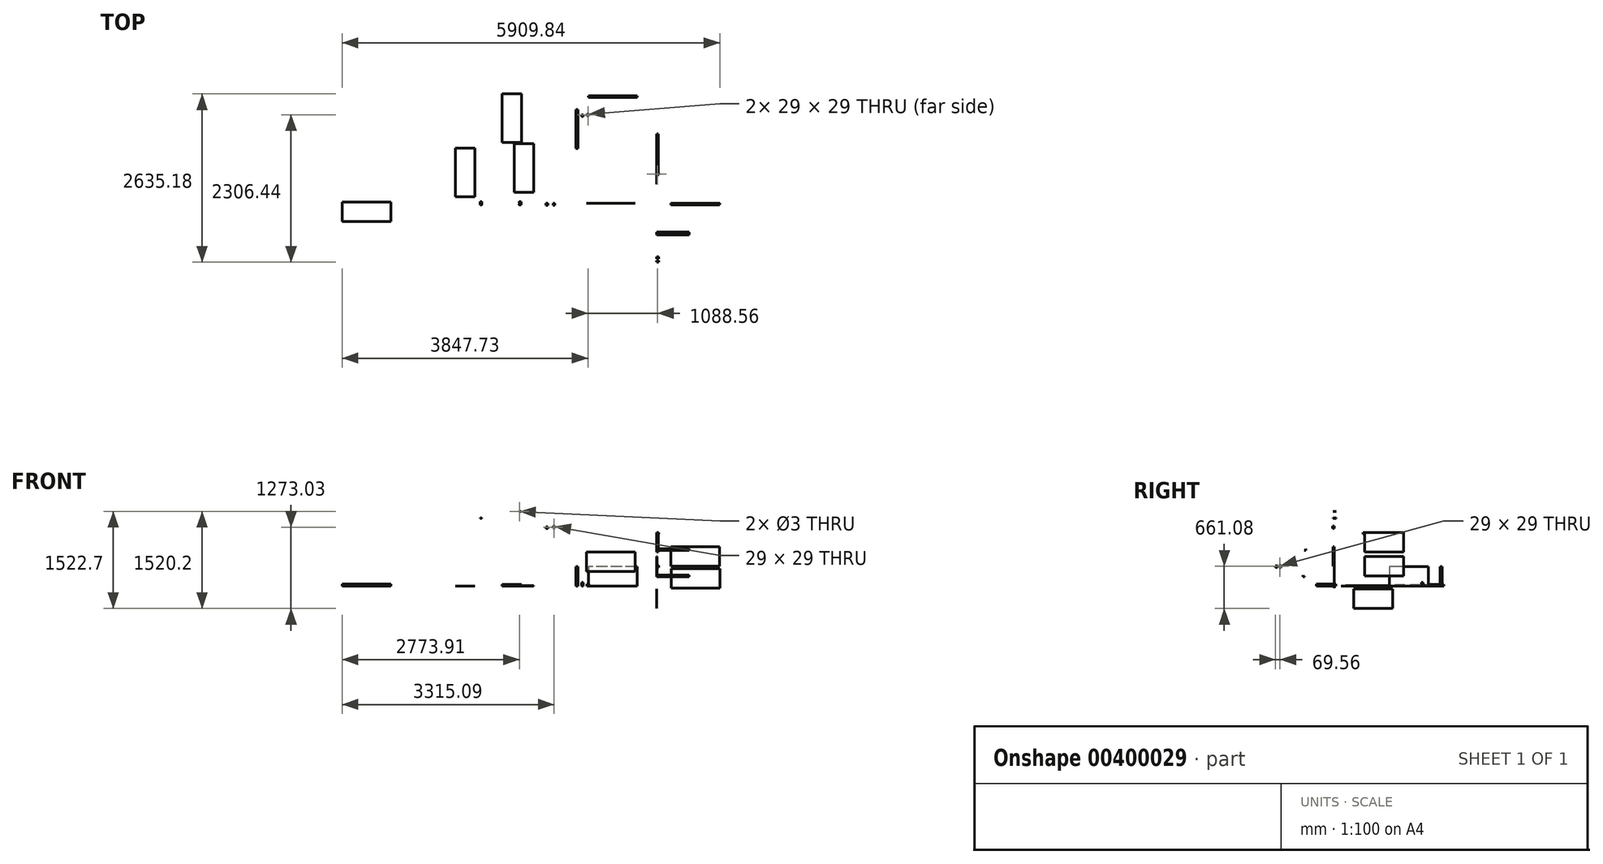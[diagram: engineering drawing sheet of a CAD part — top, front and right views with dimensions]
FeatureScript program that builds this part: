
annotation { "Feature Type Name" : "Feature", "Feature Type Description" : "" }
export const myFeature = defineFeature(function(context is Context, id is Id, definition is map)
    precondition{}
    {
        {
            var Q0;
            Q0=qCreatedBy(makeId("Front.planeOp"),FACE);
            var sketch = newSketch(context, id + "F0", { "sketchPlane" : qUnion([Q0])});
            skLineSegment(sketch, "E0.bottom", {"start": v(980.84, 309.69) * mm, "end": v(218.84, 309.69) * mm});
            skLineSegment(sketch, "E0.top", {"start": v(980.84, 614.49) * mm, "end": v(218.84, 614.49) * mm});
            skLineSegment(sketch, "E0.left", {"start": v(980.84, 309.69) * mm, "end": v(980.84, 614.49) * mm});
            skLineSegment(sketch, "E0.right", {"start": v(218.84, 309.69) * mm, "end": v(218.84, 614.49) * mm});
            skPoint(sketch, "E0.middle", {"position": v(599.84, 462.09) * mm});
            skSolve(sketch);
        }
        {
            var Q0;
            Q0=makeQuery(id+"F0.imprint","IMPRINT",FACE,{"disambiguationData":[TD([[makeQuery(id+"F0.imprint","IMPRINT",EDGE,{"derivedFrom":sQuery(id+"F0.wireOp",EDGE,"E0.bottom")}),-1.0]])]});
            extrude(context, id + "F1", {"entities" : qUnion([Q0]), "depth" : 25 * mm});
        }
        {
            var Q0;
            Q0=qCreatedBy(makeId("Front.planeOp"),FACE);
            var sketch = newSketch(context, id + "F2", { "sketchPlane" : qUnion([Q0])});
            skLineSegment(sketch, "E1.bottom", {"start": v(986.05, -29.83) * mm, "end": v(224.05, -29.83) * mm});
            skLineSegment(sketch, "E1.top", {"start": v(986.05, 274.97) * mm, "end": v(224.05, 274.97) * mm});
            skLineSegment(sketch, "E1.left", {"start": v(986.05, -29.83) * mm, "end": v(986.05, 274.97) * mm});
            skLineSegment(sketch, "E1.right", {"start": v(224.05, -29.83) * mm, "end": v(224.05, 274.97) * mm});
            skPoint(sketch, "E1.middle", {"position": v(605.05, 122.57) * mm});
            skSolve(sketch);
        }
        {
            var Q0;
            Q0=makeQuery(id+"F2.imprint","IMPRINT",FACE,{"disambiguationData":[TD([[makeQuery(id+"F2.imprint","IMPRINT",EDGE,{"derivedFrom":sQuery(id+"F2.wireOp",EDGE,"E1.bottom")}),-1.0]])]});
            extrude(context, id + "F3", {"entities" : qUnion([Q0]), "depth" : 4 * mm});
        }
        {
            var Q0;
            Q0=qCreatedBy(makeId("Front.planeOp"),FACE);
            var sketch = newSketch(context, id + "F4", { "sketchPlane" : qUnion([Q0])});
            skLineSegment(sketch, "E2.bottom", {"start": v(-340.18, 230.94) * mm, "end": v(-1102.18, 230.94) * mm});
            skLineSegment(sketch, "E2.top", {"start": v(-340.18, 535.74) * mm, "end": v(-1102.18, 535.74) * mm});
            skLineSegment(sketch, "E2.left", {"start": v(-340.18, 230.94) * mm, "end": v(-340.18, 535.74) * mm});
            skLineSegment(sketch, "E2.right", {"start": v(-1102.18, 230.94) * mm, "end": v(-1102.18, 535.74) * mm});
            skPoint(sketch, "E2.middle", {"position": v(-721.18, 383.34) * mm});
            skSolve(sketch);
        }
        {
            var Q0;
            Q0=makeQuery(id+"F4.imprint","IMPRINT",FACE,{"disambiguationData":[TD([[makeQuery(id+"F4.imprint","IMPRINT",EDGE,{"derivedFrom":sQuery(id+"F4.wireOp",EDGE,"E2.bottom")}),-1.0]])]});
            extrude(context, id + "F5", {"entities" : qUnion([Q0]), "depth" : 1 * mm});
        }
        {
            var Q0;
            Q0=qCreatedBy(makeId("Right.planeOp"),FACE);
            var sketch = newSketch(context, id + "F6", { "sketchPlane" : qUnion([Q0])});
            skLineSegment(sketch, "E3.bottom", {"start": v(1084.04, 535.01) * mm, "end": v(474.44, 535.01) * mm});
            skLineSegment(sketch, "E3.top", {"start": v(1084.04, 839.81) * mm, "end": v(474.44, 839.81) * mm});
            skLineSegment(sketch, "E3.left", {"start": v(1084.04, 535.01) * mm, "end": v(1084.04, 839.81) * mm});
            skLineSegment(sketch, "E3.right", {"start": v(474.44, 535.01) * mm, "end": v(474.44, 839.81) * mm});
            skPoint(sketch, "E3.middle", {"position": v(779.24, 687.41) * mm});
            skSolve(sketch);
        }
        {
            var Q0;
            Q0=makeQuery(id+"F6.imprint","IMPRINT",FACE,{"disambiguationData":[TD([[makeQuery(id+"F6.imprint","IMPRINT",EDGE,{"derivedFrom":sQuery(id+"F6.wireOp",EDGE,"E3.bottom")}),-1.0]])]});
            extrude(context, id + "F7", {"entities" : qUnion([Q0]), "depth" : 25 * mm});
        }
        {
            var Q0;
            Q0=qCreatedBy(makeId("Right.planeOp"),FACE);
            var sketch = newSketch(context, id + "F8", { "sketchPlane" : qUnion([Q0])});
            skLineSegment(sketch, "E4.bottom", {"start": v(1082.3, 157.36) * mm, "end": v(472.7, 157.36) * mm});
            skLineSegment(sketch, "E4.top", {"start": v(1082.3, 462.16) * mm, "end": v(472.7, 462.16) * mm});
            skLineSegment(sketch, "E4.left", {"start": v(1082.3, 157.36) * mm, "end": v(1082.3, 462.16) * mm});
            skLineSegment(sketch, "E4.right", {"start": v(472.7, 157.36) * mm, "end": v(472.7, 462.16) * mm});
            skPoint(sketch, "E4.middle", {"position": v(777.5, 309.76) * mm});
            skSolve(sketch);
        }
        {
            var Q0;
            Q0=makeQuery(id+"F8.imprint","IMPRINT",FACE,{"disambiguationData":[TD([[makeQuery(id+"F8.imprint","IMPRINT",EDGE,{"derivedFrom":sQuery(id+"F8.wireOp",EDGE,"E4.bottom")}),-1.0]])]});
            extrude(context, id + "F9", {"entities" : qUnion([Q0]), "depth" : 4 * mm});
        }
        {
            var Q0;
            Q0=qCreatedBy(makeId("Right.planeOp"),FACE);
            var sketch = newSketch(context, id + "F10", { "sketchPlane" : qUnion([Q0])});
            skLineSegment(sketch, "E5.bottom", {"start": v(910.2, -350.78) * mm, "end": v(300.6, -350.78) * mm});
            skLineSegment(sketch, "E5.top", {"start": v(910.2, -45.98) * mm, "end": v(300.6, -45.98) * mm});
            skLineSegment(sketch, "E5.left", {"start": v(910.2, -350.78) * mm, "end": v(910.2, -45.98) * mm});
            skLineSegment(sketch, "E5.right", {"start": v(300.6, -350.78) * mm, "end": v(300.6, -45.98) * mm});
            skPoint(sketch, "E5.middle", {"position": v(605.4, -198.38) * mm});
            skSolve(sketch);
        }
        {
            var Q0;
            Q0=makeQuery(id+"F10.imprint","IMPRINT",FACE,{"disambiguationData":[TD([[makeQuery(id+"F10.imprint","IMPRINT",EDGE,{"derivedFrom":sQuery(id+"F10.wireOp",EDGE,"E5.bottom")}),-1.0]])]});
            extrude(context, id + "F11", {"entities" : qUnion([Q0]), "depth" : 1 * mm});
        }
        {
            var Q0;
            Q0=qCreatedBy(makeId("Right.planeOp"),FACE);
            var sketch = newSketch(context, id + "F12", { "sketchPlane" : qUnion([Q0])});
            skLineSegment(sketch, "E6", {"start": v(-495.1, 174.65) * mm, "end": v(-495.1, 149.25) * mm});
            skLineSegment(sketch, "E7", {"start": v(-495.1, 149.25) * mm, "end": v(-469.7, 149.25) * mm});
            skLineSegment(sketch, "E8", {"start": v(-469.7, 149.25) * mm, "end": v(-469.7, 151.25) * mm});
            skLineSegment(sketch, "E9", {"start": v(-469.7, 151.25) * mm, "end": v(-493.1, 151.25) * mm});
            skLineSegment(sketch, "E10", {"start": v(-493.1, 151.25) * mm, "end": v(-493.1, 174.65) * mm});
            skLineSegment(sketch, "E11", {"start": v(-493.1, 174.65) * mm, "end": v(-495.1, 174.65) * mm});
            skSolve(sketch);
        }
        {
            var Q0;
            Q0=makeQuery(id+"F12.imprint","IMPRINT",FACE,{"disambiguationData":[TD([[makeQuery(id+"F12.imprint","IMPRINT",EDGE,{"derivedFrom":sQuery(id+"F12.wireOp",EDGE,"E6")}),1.0]])]});
            extrude(context, id + "F13", {"entities" : qUnion([Q0]), "depth" : 508 * mm});
        }
        {
            var Q0;
            Q0=qCreatedBy(makeId("Right.planeOp"),FACE);
            var sketch = newSketch(context, id + "F14", { "sketchPlane" : qUnion([Q0])});
            skLineSegment(sketch, "E12", {"start": v(-447.15, 585.76) * mm, "end": v(-447.15, 560.36) * mm});
            skLineSegment(sketch, "E13", {"start": v(-447.15, 560.36) * mm, "end": v(-472.55, 560.36) * mm});
            skLineSegment(sketch, "E14", {"start": v(-472.55, 560.36) * mm, "end": v(-472.55, 562.36) * mm});
            skLineSegment(sketch, "E15", {"start": v(-472.55, 562.36) * mm, "end": v(-449.15, 562.36) * mm});
            skLineSegment(sketch, "E16", {"start": v(-449.15, 562.36) * mm, "end": v(-449.15, 585.76) * mm});
            skLineSegment(sketch, "E17", {"start": v(-449.15, 585.76) * mm, "end": v(-447.15, 585.76) * mm});
            skSolve(sketch);
        }
        {
            var Q0;
            Q0=makeQuery(id+"F14.imprint","IMPRINT",FACE,{"disambiguationData":[TD([[makeQuery(id+"F14.imprint","IMPRINT",EDGE,{"derivedFrom":sQuery(id+"F14.wireOp",EDGE,"E12")}),-1.0]])]});
            var Q1;
            Q1=sQuery(id+"F14.wireOp",EDGE,"E15");
            extrude(context, id + "F15", {"entities" : qUnion([Q0]), "surfaceEntities" : qUnion([Q1]), "depth" : 508 * mm});
        }
        {
            var Q0;
            Q0=qCreatedBy(makeId("Top.planeOp"),FACE);
            var sketch = newSketch(context, id + "F16", { "sketchPlane" : qUnion([Q0])});
            skLineSegment(sketch, "E18.bottom", {"start": v(-2119.67, 951.73) * mm, "end": v(-2424.47, 951.73) * mm});
            skLineSegment(sketch, "E18.top", {"start": v(-2119.67, 1713.73) * mm, "end": v(-2424.47, 1713.73) * mm});
            skLineSegment(sketch, "E18.left", {"start": v(-2119.67, 951.73) * mm, "end": v(-2119.67, 1713.73) * mm});
            skLineSegment(sketch, "E18.right", {"start": v(-2424.47, 951.73) * mm, "end": v(-2424.47, 1713.73) * mm});
            skPoint(sketch, "E18.middle", {"position": v(-2272.07, 1332.73) * mm});
            skSolve(sketch);
        }
        {
            var Q0;
            Q0=makeQuery(id+"F16.imprint","IMPRINT",FACE,{"disambiguationData":[TD([[makeQuery(id+"F16.imprint","IMPRINT",EDGE,{"derivedFrom":sQuery(id+"F16.wireOp",EDGE,"E18.bottom")}),-1.0]])]});
            extrude(context, id + "F17", {"entities" : qUnion([Q0]), "depth" : 25 * mm});
        }
        {
            var Q0;
            Q0=qCreatedBy(makeId("Top.planeOp"),FACE);
            var sketch = newSketch(context, id + "F18", { "sketchPlane" : qUnion([Q0])});
            skLineSegment(sketch, "E19.bottom", {"start": v(-2849.46, 102.13) * mm, "end": v(-3154.26, 102.13) * mm});
            skLineSegment(sketch, "E19.top", {"start": v(-2849.46, 864.13) * mm, "end": v(-3154.26, 864.13) * mm});
            skLineSegment(sketch, "E19.left", {"start": v(-2849.46, 102.13) * mm, "end": v(-2849.46, 864.13) * mm});
            skLineSegment(sketch, "E19.right", {"start": v(-3154.26, 102.13) * mm, "end": v(-3154.26, 864.13) * mm});
            skPoint(sketch, "E19.middle", {"position": v(-3001.86, 483.13) * mm});
            skSolve(sketch);
        }
        {
            var Q0;
            Q0=makeQuery(id+"F18.imprint","IMPRINT",FACE,{"disambiguationData":[TD([[makeQuery(id+"F18.imprint","IMPRINT",EDGE,{"derivedFrom":sQuery(id+"F18.wireOp",EDGE,"E19.bottom")}),-1.0]])]});
            extrude(context, id + "F19", {"entities" : qUnion([Q0]), "depth" : 1 * mm});
        }
        {
            var Q0;
            Q0=qCreatedBy(makeId("Top.planeOp"),FACE);
            var sketch = newSketch(context, id + "F20", { "sketchPlane" : qUnion([Q0])});
            skLineSegment(sketch, "E20.bottom", {"start": v(-1923.09, 173.05) * mm, "end": v(-2227.89, 173.05) * mm});
            skLineSegment(sketch, "E20.top", {"start": v(-1923.09, 935.05) * mm, "end": v(-2227.89, 935.05) * mm});
            skLineSegment(sketch, "E20.left", {"start": v(-1923.09, 173.05) * mm, "end": v(-1923.09, 935.05) * mm});
            skLineSegment(sketch, "E20.right", {"start": v(-2227.89, 173.05) * mm, "end": v(-2227.89, 935.05) * mm});
            skPoint(sketch, "E20.middle", {"position": v(-2075.49, 554.05) * mm});
            skSolve(sketch);
        }
        {
            var Q0;
            Q0=makeQuery(id+"F20.imprint","IMPRINT",FACE,{"disambiguationData":[TD([[makeQuery(id+"F20.imprint","IMPRINT",EDGE,{"derivedFrom":sQuery(id+"F20.wireOp",EDGE,"E20.bottom")}),-1.0]])]});
            extrude(context, id + "F21", {"entities" : qUnion([Q0]), "depth" : 4 * mm});
        }
        {
            var Q0;
            Q0=qCreatedBy(makeId("Front.planeOp"),FACE);
            var sketch = newSketch(context, id + "F22", { "sketchPlane" : qUnion([Q0])});
            skCircle(sketch, "E21", {"center": v(-2743.03, 1064.39) * mm, "radius": 2.5 * mm});
            skCircle(sketch, "E22", {"center": v(-2743.03, 1064.39) * mm, "radius": 1.5 * mm});
            skSolve(sketch);
        }
        {
            var Q0;
            Q0=makeQuery(id+"F22.imprint","IMPRINT",FACE,{"disambiguationData":[TD([[makeQuery(id+"F22.imprint","IMPRINT",EDGE,{"derivedFrom":sQuery(id+"F22.wireOp",EDGE,"E21")}),1.0]])]});
            extrude(context, id + "F23", {"entities" : qUnion([Q0]), "endBound" : BoundingType.SYMMETRIC, "depth" : 25.4 * mm});
        }
        {
            var Q0;
            Q0=makeQuery(id+"F22.imprint","IMPRINT",FACE,{"disambiguationData":[TD([[makeQuery(id+"F22.imprint","IMPRINT",EDGE,{"derivedFrom":sQuery(id+"F22.wireOp",EDGE,"E22")}),1.0]])]});
            extrude(context, id + "F24", {"entities" : qUnion([Q0]), "operationType" : NewBodyOperationType.ADD, "endBound" : BoundingType.SYMMETRIC, "depth" : 50.8 * mm});
        }
        {
            var Q0;
            Q0=makeQuery(id+"F23.opExtrude","CAP_FACE",FACE,{"disambiguationData":[OSD([sQuery(id+"F22.wireOp",EDGE,"E21"),sQuery(id+"F22.wireOp",EDGE,"E22")])],"isStart":true});
            var sketch = newSketch(context, id + "F25", { "sketchPlane" : qUnion([Q0])});
            skLineSegment(sketch, "E23", {"start": v(2744.81, 1066.14) * mm, "end": v(2744.81, 1062.64) * mm});
            skLineSegment(sketch, "E24", {"start": v(2744.81, 1062.64) * mm, "end": v(2746.81, 1062.64) * mm});
            skLineSegment(sketch, "E25", {"start": v(2746.81, 1062.64) * mm, "end": v(2746.81, 1066.14) * mm});
            skLineSegment(sketch, "E26", {"start": v(2746.81, 1066.14) * mm, "end": v(2744.81, 1066.14) * mm});
            skSolve(sketch);
        }
        {
            var Q0;
            {var subQ0=sQuery(id+"F25.wireOp",EDGE,"E24");Q0=makeQuery(id+"F25.imprint","IMPRINT",FACE,{"disambiguationData":[TD([[makeQuery(id+"F25.imprint","IMPRINT",EDGE,{"derivedFrom":subQ0}),1.0]])]});}
            extrude(context, id + "F26", {"entities" : qUnion([Q0]), "oppositeDirection" : true, "depth" : 25.4 * mm});
        }
        {
            var Q0;
            Q0=makeQuery(id+"F22.imprint","IMPRINT",FACE,{"disambiguationData":[TD([[makeQuery(id+"F22.imprint","IMPRINT",EDGE,{"derivedFrom":sQuery(id+"F22.wireOp",EDGE,"E21")}),1.0]])]});
            var sketch = newSketch(context, id + "F27", { "sketchPlane" : qUnion([Q0])});
            skLineSegment(sketch, "E27.bottom", {"start": v(-2746.81, 1066.14) * mm, "end": v(-2765.86, 1066.14) * mm});
            skLineSegment(sketch, "E27.top", {"start": v(-2746.81, 1062.64) * mm, "end": v(-2765.86, 1062.64) * mm});
            skLineSegment(sketch, "E27.left", {"start": v(-2746.81, 1066.14) * mm, "end": v(-2746.81, 1062.64) * mm});
            skLineSegment(sketch, "E27.right", {"start": v(-2765.86, 1066.14) * mm, "end": v(-2765.86, 1062.64) * mm});
            skSolve(sketch);
        }
        {
            var Q0;
            Q0=makeQuery(id+"F27.imprint","IMPRINT",FACE,{"disambiguationData":[TD([[makeQuery(id+"F27.imprint","IMPRINT",EDGE,{"derivedFrom":sQuery(id+"F27.wireOp",EDGE,"E27.bottom")}),1.0]])]});
            extrude(context, id + "F28", {"entities" : qUnion([Q0]), "operationType" : NewBodyOperationType.ADD, "endBound" : BoundingType.SYMMETRIC, "depth" : 50.8 * mm});
        }
        {
            var Q0;
            Q0=qCreatedBy(makeId("Front.planeOp"),FACE);
            var sketch = newSketch(context, id + "F29", { "sketchPlane" : qUnion([Q0])});
            skCircle(sketch, "E28", {"center": v(-2149.88, 1169.42) * mm, "radius": 2.5 * mm});
            skCircle(sketch, "E29", {"center": v(-2149.88, 1169.42) * mm, "radius": 1.5 * mm});
            skSolve(sketch);
        }
        {
            var Q0;
            Q0=makeQuery(id+"F29.imprint","IMPRINT",FACE,{"disambiguationData":[TD([[makeQuery(id+"F29.imprint","IMPRINT",EDGE,{"derivedFrom":sQuery(id+"F29.wireOp",EDGE,"E28")}),1.0]])]});
            extrude(context, id + "F30", {"entities" : qUnion([Q0]), "endBound" : BoundingType.SYMMETRIC, "depth" : 50.8 * mm});
        }
        {
            var Q0;
            Q0=makeQuery(id+"F29.imprint","IMPRINT",FACE,{"disambiguationData":[TD([[makeQuery(id+"F29.imprint","IMPRINT",EDGE,{"derivedFrom":sQuery(id+"F29.wireOp",EDGE,"E28")}),1.0]])]});
            extrude(context, id + "F31", {"entities" : qUnion([Q0]), "operationType" : NewBodyOperationType.REMOVE, "endBound" : BoundingType.SYMMETRIC, "oppositeDirection" : true, "depth" : 25.4 * mm});
        }
        {
            var Q0;
            Q0=makeQuery(id+"F29.imprint","IMPRINT",FACE,{"disambiguationData":[TD([[makeQuery(id+"F29.imprint","IMPRINT",EDGE,{"derivedFrom":sQuery(id+"F29.wireOp",EDGE,"E29")}),1.0]])]});
            var sketch = newSketch(context, id + "F32", { "sketchPlane" : qUnion([Q0])});
            skLineSegment(sketch, "E30", {"start": v(-2148.18, 1171.13) * mm, "end": v(-2148.18, 1167.63) * mm});
            skLineSegment(sketch, "E31", {"start": v(-2148.18, 1167.63) * mm, "end": v(-2146.18, 1167.63) * mm});
            skLineSegment(sketch, "E32", {"start": v(-2146.18, 1167.63) * mm, "end": v(-2146.18, 1171.13) * mm});
            skLineSegment(sketch, "E33", {"start": v(-2146.18, 1171.13) * mm, "end": v(-2148.18, 1171.13) * mm});
            skSolve(sketch);
        }
        {
            var Q0;
            Q0=makeQuery(id+"F32.imprint","IMPRINT",FACE,{"disambiguationData":[TD([[makeQuery(id+"F32.imprint","IMPRINT",EDGE,{"derivedFrom":sQuery(id+"F32.wireOp",EDGE,"E30")}),1.0]])]});
            extrude(context, id + "F33", {"entities" : qUnion([Q0]), "endBound" : BoundingType.SYMMETRIC, "depth" : 50.8 * mm});
        }
        {
            var Q0;
            Q0=makeQuery(id+"F32.imprint","IMPRINT",FACE,{"disambiguationData":[TD([[makeQuery(id+"F32.imprint","IMPRINT",EDGE,{"derivedFrom":sQuery(id+"F32.wireOp",EDGE,"E30")}),1.0]])]});
            extrude(context, id + "F34", {"entities" : qUnion([Q0]), "operationType" : NewBodyOperationType.REMOVE, "endBound" : BoundingType.SYMMETRIC, "oppositeDirection" : true, "depth" : 25.4 * mm});
        }
        {
            var Q0;
            Q0=makeQuery(id+"F33.opExtrude","CAP_FACE",FACE,{"disambiguationData":[OSD([sQuery(id+"F32.wireOp",EDGE,"E30"),sQuery(id+"F32.wireOp",EDGE,"E31"),sQuery(id+"F32.wireOp",EDGE,"E32"),sQuery(id+"F32.wireOp",EDGE,"E33")])],"isStart":false});
            var sketch = newSketch(context, id + "F35", { "sketchPlane" : qUnion([Q0])});
            skLineSegment(sketch, "E34.bottom", {"start": v(-2146.18, 1171.13) * mm, "end": v(-2120.78, 1171.13) * mm});
            skLineSegment(sketch, "E34.top", {"start": v(-2146.18, 1167.63) * mm, "end": v(-2120.78, 1167.63) * mm});
            skLineSegment(sketch, "E34.left", {"start": v(-2146.18, 1171.13) * mm, "end": v(-2146.18, 1167.63) * mm});
            skLineSegment(sketch, "E34.right", {"start": v(-2120.78, 1171.13) * mm, "end": v(-2120.78, 1167.63) * mm});
            skSolve(sketch);
        }
        {
            var Q0;
            Q0=makeQuery(id+"F35.imprint","IMPRINT",FACE,{"disambiguationData":[TD([[makeQuery(id+"F35.imprint","IMPRINT",EDGE,{"derivedFrom":sQuery(id+"F35.wireOp",EDGE,"E34.bottom")}),-1.0]])]});
            extrude(context, id + "F36", {"entities" : qUnion([Q0]), "oppositeDirection" : true, "depth" : 50.8 * mm});
        }
        {
            var Q0;
            Q0=makeQuery(id+"F7.opExtrude","SWEPT_FACE",FACE,{"disambiguationData":[OSD([sQuery(id+"F6.wireOp",EDGE,"E3.top")])]});
            var sketch = newSketch(context, id + "F37", { "sketchPlane" : qUnion([Q0])});
            skLineSegment(sketch, "E35.bottom", {"start": v(27.5, 444.44) * mm, "end": v(-2.5, 444.44) * mm});
            skLineSegment(sketch, "E35.top", {"start": v(27.5, 474.44) * mm, "end": v(-2.5, 474.44) * mm});
            skLineSegment(sketch, "E35.left", {"start": v(27.5, 444.44) * mm, "end": v(27.5, 474.44) * mm});
            skLineSegment(sketch, "E35.right", {"start": v(-2.5, 444.44) * mm, "end": v(-2.5, 474.44) * mm});
            skPoint(sketch, "E35.middle", {"position": v(12.5, 459.44) * mm});
            skLineSegment(sketch, "E36.bottom", {"start": v(27, 444.94) * mm, "end": v(-2, 444.94) * mm});
            skLineSegment(sketch, "E36.top", {"start": v(27, 473.94) * mm, "end": v(-2, 473.94) * mm});
            skLineSegment(sketch, "E36.left", {"start": v(27, 444.94) * mm, "end": v(27, 473.94) * mm});
            skLineSegment(sketch, "E36.right", {"start": v(-2, 444.94) * mm, "end": v(-2, 473.94) * mm});
            skSolve(sketch);
        }
        {
            var Q0;
            Q0=makeQuery(id+"F37.imprint","IMPRINT",FACE,{"disambiguationData":[TD([[makeQuery(id+"F37.imprint","IMPRINT",EDGE,{"derivedFrom":sQuery(id+"F37.wireOp",EDGE,"E35.bottom")}),-1.0]])]});
            extrude(context, id + "F38", {"entities" : qUnion([Q0]), "operationType" : NewBodyOperationType.ADD, "oppositeDirection" : true, "depth" : 25.4 * mm});
        }
        {
            var Q0;
            Q0=qCreatedBy(makeId("Top.planeOp"),FACE);
            var sketch = newSketch(context, id + "F39", { "sketchPlane" : qUnion([Q0])});
            skLineSegment(sketch, "E37.bottom", {"start": v(-1150.64, 1359.3) * mm, "end": v(-1178.64, 1359.3) * mm});
            skLineSegment(sketch, "E37.top", {"start": v(-1150.64, 1387.3) * mm, "end": v(-1178.64, 1387.3) * mm});
            skLineSegment(sketch, "E37.left", {"start": v(-1150.64, 1359.3) * mm, "end": v(-1150.64, 1387.3) * mm});
            skLineSegment(sketch, "E37.right", {"start": v(-1178.64, 1359.3) * mm, "end": v(-1178.64, 1387.3) * mm});
            skPoint(sketch, "E37.middle", {"position": v(-1164.64, 1373.3) * mm});
            skSolve(sketch);
        }
        {
            var Q0;
            Q0=makeQuery(id+"F39.imprint","IMPRINT",FACE,{"disambiguationData":[TD([[makeQuery(id+"F39.imprint","IMPRINT",EDGE,{"derivedFrom":sQuery(id+"F39.wireOp",EDGE,"E37.bottom")}),-1.0]])]});
            extrude(context, id + "F40", {"entities" : qUnion([Q0]), "depth" : 60 * mm});
        }
        {
            var Q0;
            Q0=qCreatedBy(makeId("Top.planeOp"),FACE);
            var sketch = newSketch(context, id + "F41", { "sketchPlane" : qUnion([Q0])});
            skLineSegment(sketch, "E38.bottom", {"start": v(-1061.06, 1370) * mm, "end": v(-1091.06, 1370) * mm});
            skLineSegment(sketch, "E38.top", {"start": v(-1061.06, 1400) * mm, "end": v(-1091.06, 1400) * mm});
            skLineSegment(sketch, "E38.left", {"start": v(-1061.06, 1370) * mm, "end": v(-1061.06, 1400) * mm});
            skLineSegment(sketch, "E38.right", {"start": v(-1091.06, 1370) * mm, "end": v(-1091.06, 1400) * mm});
            skPoint(sketch, "E38.middle", {"position": v(-1076.06, 1385) * mm});
            skLineSegment(sketch, "E39.bottom", {"start": v(-1061.56, 1370.5) * mm, "end": v(-1090.56, 1370.5) * mm});
            skLineSegment(sketch, "E39.top", {"start": v(-1061.56, 1399.5) * mm, "end": v(-1090.56, 1399.5) * mm});
            skLineSegment(sketch, "E39.left", {"start": v(-1061.56, 1370.5) * mm, "end": v(-1061.56, 1399.5) * mm});
            skLineSegment(sketch, "E39.right", {"start": v(-1090.56, 1370.5) * mm, "end": v(-1090.56, 1399.5) * mm});
            skSolve(sketch);
        }
        {
            var Q0;
            Q0=makeQuery(id+"F41.imprint","IMPRINT",FACE,{"disambiguationData":[TD([[makeQuery(id+"F41.imprint","IMPRINT",EDGE,{"derivedFrom":sQuery(id+"F41.wireOp",EDGE,"E38.bottom")}),-1.0]])]});
            extrude(context, id + "F42", {"entities" : qUnion([Q0]), "depth" : 30 * mm});
        }
        {
            var Q0;
            Q0=qCreatedBy(makeId("Top.planeOp"),FACE);
            var sketch = newSketch(context, id + "F43", { "sketchPlane" : qUnion([Q0])});
            skLineSegment(sketch, "E40.bottom", {"start": v(-1234.3, 1468.82) * mm, "end": v(-1264.3, 1468.82) * mm});
            skLineSegment(sketch, "E40.top", {"start": v(-1234.3, 859.22) * mm, "end": v(-1264.3, 859.22) * mm});
            skLineSegment(sketch, "E40.left", {"start": v(-1234.3, 1468.82) * mm, "end": v(-1234.3, 859.22) * mm});
            skLineSegment(sketch, "E40.right", {"start": v(-1264.3, 1468.82) * mm, "end": v(-1264.3, 859.22) * mm});
            skPoint(sketch, "E40.middle", {"position": v(-1249.3, 1164.02) * mm});
            skSolve(sketch);
        }
        {
            var Q0;
            Q0=makeQuery(id+"F43.imprint","IMPRINT",FACE,{"disambiguationData":[TD([[makeQuery(id+"F43.imprint","IMPRINT",EDGE,{"derivedFrom":sQuery(id+"F43.wireOp",EDGE,"E40.bottom")}),1.0]])]});
            extrude(context, id + "F44", {"entities" : qUnion([Q0]), "depth" : 304.8 * mm});
        }
        {
            var Q0;
            Q0=qCreatedBy(makeId("Top.planeOp"),FACE);
            var sketch = newSketch(context, id + "F45", { "sketchPlane" : qUnion([Q0])});
            skLineSegment(sketch, "E41.bottom", {"start": v(-309.44, 1655.47) * mm, "end": v(-1071.44, 1655.47) * mm});
            skLineSegment(sketch, "E41.top", {"start": v(-309.44, 1685.47) * mm, "end": v(-1071.44, 1685.47) * mm});
            skLineSegment(sketch, "E41.left", {"start": v(-309.44, 1655.47) * mm, "end": v(-309.44, 1685.47) * mm});
            skLineSegment(sketch, "E41.right", {"start": v(-1071.44, 1655.47) * mm, "end": v(-1071.44, 1685.47) * mm});
            skPoint(sketch, "E41.middle", {"position": v(-690.44, 1670.47) * mm});
            skSolve(sketch);
        }
        {
            var Q0;
            Q0=makeQuery(id+"F45.imprint","IMPRINT",FACE,{"disambiguationData":[TD([[makeQuery(id+"F45.imprint","IMPRINT",EDGE,{"derivedFrom":sQuery(id+"F45.wireOp",EDGE,"E41.bottom")}),-1.0]])]});
            extrude(context, id + "F46", {"entities" : qUnion([Q0]), "depth" : 304.8 * mm});
        }
        {
            var Q0;
            Q0=qCreatedBy(makeId("Front.planeOp"),FACE);
            var sketch = newSketch(context, id + "F47", { "sketchPlane" : qUnion([Q0])});
            skLineSegment(sketch, "E42.bottom", {"start": v(-1706.5, 902.3) * mm, "end": v(-1734.5, 902.3) * mm});
            skLineSegment(sketch, "E42.top", {"start": v(-1706.5, 930.3) * mm, "end": v(-1734.5, 930.3) * mm});
            skLineSegment(sketch, "E42.left", {"start": v(-1706.5, 902.3) * mm, "end": v(-1706.5, 930.3) * mm});
            skLineSegment(sketch, "E42.right", {"start": v(-1734.5, 902.3) * mm, "end": v(-1734.5, 930.3) * mm});
            skPoint(sketch, "E42.middle", {"position": v(-1720.5, 916.3) * mm});
            skSolve(sketch);
        }
        {
            var Q0;
            Q0=makeQuery(id+"F47.imprint","IMPRINT",FACE,{"disambiguationData":[TD([[makeQuery(id+"F47.imprint","IMPRINT",EDGE,{"derivedFrom":sQuery(id+"F47.wireOp",EDGE,"E42.bottom")}),-1.0]])]});
            extrude(context, id + "F48", {"entities" : qUnion([Q0]), "depth" : 30 * mm});
        }
        {
            var Q0;
            Q0=qCreatedBy(makeId("Front.planeOp"),FACE);
            var sketch = newSketch(context, id + "F49", { "sketchPlane" : qUnion([Q0])});
            skLineSegment(sketch, "E43.bottom", {"start": v(-1593.7, 907.25) * mm, "end": v(-1623.7, 907.25) * mm});
            skLineSegment(sketch, "E43.top", {"start": v(-1593.7, 937.25) * mm, "end": v(-1623.7, 937.25) * mm});
            skLineSegment(sketch, "E43.left", {"start": v(-1593.7, 907.25) * mm, "end": v(-1593.7, 937.25) * mm});
            skLineSegment(sketch, "E43.right", {"start": v(-1623.7, 907.25) * mm, "end": v(-1623.7, 937.25) * mm});
            skPoint(sketch, "E43.middle", {"position": v(-1608.7, 922.25) * mm});
            skLineSegment(sketch, "E44.bottom", {"start": v(-1594.2, 907.75) * mm, "end": v(-1623.2, 907.75) * mm});
            skLineSegment(sketch, "E44.top", {"start": v(-1594.2, 936.75) * mm, "end": v(-1623.2, 936.75) * mm});
            skLineSegment(sketch, "E44.left", {"start": v(-1594.2, 907.75) * mm, "end": v(-1594.2, 936.75) * mm});
            skLineSegment(sketch, "E44.right", {"start": v(-1623.2, 907.75) * mm, "end": v(-1623.2, 936.75) * mm});
            skSolve(sketch);
        }
        {
            var Q0;
            Q0=makeQuery(id+"F49.imprint","IMPRINT",FACE,{"disambiguationData":[TD([[makeQuery(id+"F49.imprint","IMPRINT",EDGE,{"derivedFrom":sQuery(id+"F49.wireOp",EDGE,"E43.bottom")}),-1.0]])]});
            extrude(context, id + "F50", {"entities" : qUnion([Q0]), "depth" : 30 * mm});
        }
        {
            var Q0;
            Q0=qCreatedBy(makeId("Right.planeOp"),FACE);
            var sketch = newSketch(context, id + "F51", { "sketchPlane" : qUnion([Q0])});
            skLineSegment(sketch, "E45.bottom", {"start": v(-893.45, 292.3) * mm, "end": v(-921.45, 292.3) * mm});
            skLineSegment(sketch, "E45.top", {"start": v(-893.45, 320.3) * mm, "end": v(-921.45, 320.3) * mm});
            skLineSegment(sketch, "E45.left", {"start": v(-893.45, 292.3) * mm, "end": v(-893.45, 320.3) * mm});
            skLineSegment(sketch, "E45.right", {"start": v(-921.45, 292.3) * mm, "end": v(-921.45, 320.3) * mm});
            skPoint(sketch, "E45.middle", {"position": v(-907.45, 306.3) * mm});
            skSolve(sketch);
        }
        {
            var Q0;
            Q0=makeQuery(id+"F51.imprint","IMPRINT",FACE,{"disambiguationData":[TD([[makeQuery(id+"F51.imprint","IMPRINT",EDGE,{"derivedFrom":sQuery(id+"F51.wireOp",EDGE,"E45.bottom")}),-1.0]])]});
            extrude(context, id + "F52", {"entities" : qUnion([Q0]), "depth" : 30 * mm});
        }
        {
            var Q0;
            Q0=qCreatedBy(makeId("Right.planeOp"),FACE);
            var sketch = newSketch(context, id + "F53", { "sketchPlane" : qUnion([Q0])});
            skLineSegment(sketch, "E46.bottom", {"start": v(-836.9, 295.3) * mm, "end": v(-866.9, 295.3) * mm});
            skLineSegment(sketch, "E46.top", {"start": v(-836.9, 325.3) * mm, "end": v(-866.9, 325.3) * mm});
            skLineSegment(sketch, "E46.left", {"start": v(-836.9, 295.3) * mm, "end": v(-836.9, 325.3) * mm});
            skLineSegment(sketch, "E46.right", {"start": v(-866.9, 295.3) * mm, "end": v(-866.9, 325.3) * mm});
            skPoint(sketch, "E46.middle", {"position": v(-851.9, 310.3) * mm});
            skLineSegment(sketch, "E47.bottom", {"start": v(-837.4, 295.8) * mm, "end": v(-866.4, 295.8) * mm});
            skLineSegment(sketch, "E47.top", {"start": v(-837.4, 324.8) * mm, "end": v(-866.4, 324.8) * mm});
            skLineSegment(sketch, "E47.left", {"start": v(-837.4, 295.8) * mm, "end": v(-837.4, 324.8) * mm});
            skLineSegment(sketch, "E47.right", {"start": v(-866.4, 295.8) * mm, "end": v(-866.4, 324.8) * mm});
            skSolve(sketch);
        }
        {
            var Q0;
            Q0=makeQuery(id+"F53.imprint","IMPRINT",FACE,{"disambiguationData":[TD([[makeQuery(id+"F53.imprint","IMPRINT",EDGE,{"derivedFrom":sQuery(id+"F53.wireOp",EDGE,"E46.bottom")}),-1.0]])]});
            extrude(context, id + "F54", {"entities" : qUnion([Q0]), "depth" : 30 * mm});
        }
        {
            var Q0;
            Q0=qCreatedBy(makeId("Top.planeOp"),FACE);
            var sketch = newSketch(context, id + "F55", { "sketchPlane" : qUnion([Q0])});
            skLineSegment(sketch, "E48.bottom", {"start": v(-4161.79, -282.16) * mm, "end": v(-4923.79, -282.16) * mm});
            skLineSegment(sketch, "E48.top", {"start": v(-4161.79, 22.64) * mm, "end": v(-4923.79, 22.64) * mm});
            skLineSegment(sketch, "E48.left", {"start": v(-4161.79, -282.16) * mm, "end": v(-4161.79, 22.64) * mm});
            skLineSegment(sketch, "E48.right", {"start": v(-4923.79, -282.16) * mm, "end": v(-4923.79, 22.64) * mm});
            skPoint(sketch, "E48.middle", {"position": v(-4542.79, -129.76) * mm});
            skSolve(sketch);
        }
        {
            var Q0;
            Q0=makeQuery(id+"F55.imprint","IMPRINT",FACE,{"disambiguationData":[TD([[makeQuery(id+"F55.imprint","IMPRINT",EDGE,{"derivedFrom":sQuery(id+"F55.wireOp",EDGE,"E48.bottom")}),-1.0]])]});
            extrude(context, id + "F56", {"entities" : qUnion([Q0]), "depth" : 30 * mm});
        }
    });
